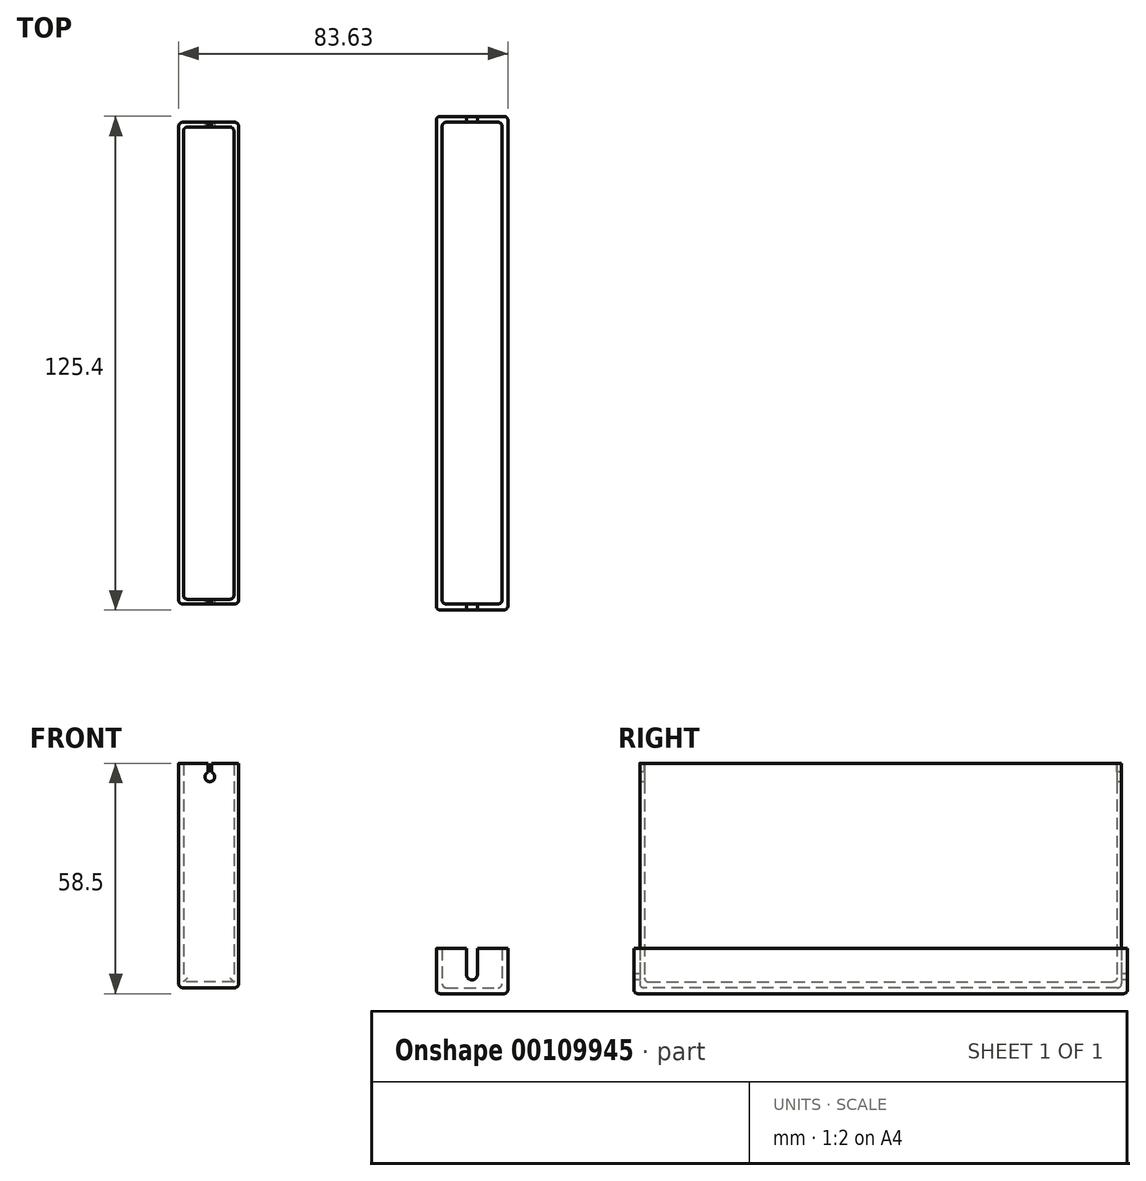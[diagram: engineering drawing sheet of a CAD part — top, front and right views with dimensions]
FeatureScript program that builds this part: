
annotation { "Feature Type Name" : "Feature", "Feature Type Description" : "" }
export const myFeature = defineFeature(function(context is Context, id is Id, definition is map)
    precondition{}
    {
        {
            var Q0;
            Q0=qCreatedBy(makeId("Top.planeOp"),FACE);
            var sketch = newSketch(context, id + "F0", { "sketchPlane" : qUnion([Q0])});
            skLineSegment(sketch, "E0.bottom", {"start": v(-47.39, 113) * mm, "end": v(-34.59, 113) * mm});
            skLineSegment(sketch, "E0.top", {"start": v(-47.39, -7) * mm, "end": v(-34.59, -7) * mm});
            skLineSegment(sketch, "E0.left", {"start": v(-47.39, 113) * mm, "end": v(-47.39, -7) * mm});
            skLineSegment(sketch, "E0.right", {"start": v(-34.59, 113) * mm, "end": v(-34.59, -7) * mm});
            skLineSegment(sketch, "E1.bottom", {"start": v(-48.59, 114.2) * mm, "end": v(-33.39, 114.2) * mm});
            skLineSegment(sketch, "E1.top", {"start": v(-48.59, -8.2) * mm, "end": v(-33.39, -8.2) * mm});
            skLineSegment(sketch, "E1.left", {"start": v(-48.59, 114.2) * mm, "end": v(-48.59, -8.2) * mm});
            skLineSegment(sketch, "E1.right", {"start": v(-33.39, 114.2) * mm, "end": v(-33.39, -8.2) * mm});
            skLineSegment(sketch, "E2.bottom", {"start": v(18.34, 114.2) * mm, "end": v(33.54, 114.2) * mm});
            skLineSegment(sketch, "E2.top", {"start": v(18.34, -8.2) * mm, "end": v(33.54, -8.2) * mm});
            skLineSegment(sketch, "E2.left", {"start": v(18.34, 114.2) * mm, "end": v(18.34, -8.2) * mm});
            skLineSegment(sketch, "E2.right", {"start": v(33.54, 114.2) * mm, "end": v(33.54, -8.2) * mm});
            skLineSegment(sketch, "E3.bottom", {"start": v(16.84, 115.7) * mm, "end": v(35.04, 115.7) * mm});
            skLineSegment(sketch, "E3.top", {"start": v(16.84, -9.7) * mm, "end": v(35.04, -9.7) * mm});
            skLineSegment(sketch, "E3.left", {"start": v(16.84, 115.7) * mm, "end": v(16.84, -9.7) * mm});
            skLineSegment(sketch, "E3.right", {"start": v(35.04, 115.7) * mm, "end": v(35.04, -9.7) * mm});
            skSolve(sketch);
        }
        {
            var Q0;
            Q0=makeQuery(id+"F0.imprint","IMPRINT",FACE,{"disambiguationData":[TD([[makeQuery(id+"F0.imprint","IMPRINT",EDGE,{"derivedFrom":sQuery(id+"F0.wireOp",EDGE,"E0.bottom")}),-1.0]])]});
            var Q1;
            Q1=makeQuery(id+"F0.imprint","IMPRINT",FACE,{"disambiguationData":[TD([[makeQuery(id+"F0.imprint","IMPRINT",EDGE,{"derivedFrom":sQuery(id+"F0.wireOp",EDGE,"E0.bottom")}),1.0]])]});
            extrude(context, id + "F1", {"entities" : qUnion([Q0, Q1]), "depth" : 1.5 * mm});
        }
        {
            var Q0;
            Q0=makeQuery(id+"F0.imprint","IMPRINT",FACE,{"disambiguationData":[TD([[makeQuery(id+"F0.imprint","IMPRINT",EDGE,{"derivedFrom":sQuery(id+"F0.wireOp",EDGE,"E0.bottom")}),1.0]])]});
            extrude(context, id + "F2", {"entities" : qUnion([Q0]), "operationType" : NewBodyOperationType.ADD, "depth" : 57 * mm});
        }
        {
            var Q0;
            {var subQ0=sQuery(id+"F0.wireOp",EDGE,"E1.top");Q0=makeQuery(id+"F2.boolean.opBoolean","MERGE",FACE,{"derivedFrom":[makeQuery(id+"F1.opExtrude","SWEPT_FACE",FACE,{"disambiguationData":[OSD([subQ0])]}),makeQuery(id+"F2.opExtrude","SWEPT_FACE",FACE,{"disambiguationData":[OSD([subQ0])]})]});}
            var sketch = newSketch(context, id + "F3", { "sketchPlane" : qUnion([Q0])});
            skCircle(sketch, "E4", {"center": v(-40.69, 53.6) * mm, "radius": 1.25 * mm});
            skLineSegment(sketch, "E5.bottom", {"start": v(-41.09, 57) * mm, "end": v(-40.29, 57) * mm});
            skLineSegment(sketch, "E5.top", {"start": v(-41.09, 53.6) * mm, "end": v(-40.29, 53.6) * mm});
            skLineSegment(sketch, "E5.left", {"start": v(-41.09, 57) * mm, "end": v(-41.09, 53.6) * mm});
            skLineSegment(sketch, "E5.right", {"start": v(-40.29, 57) * mm, "end": v(-40.29, 53.6) * mm});
            skSolve(sketch);
        }
        {
            var Q0;
            {var subQ5=sQuery(id+"F3.wireOp",EDGE,"E5.top");Q0=makeQuery(id+"F3.imprint","IMPRINT",FACE,{"disambiguationData":[TD([[makeQuery(id+"F3.imprint","IMPRINT",EDGE,{"derivedFrom":subQ5}),-1.0]])]});}
            var Q1;
            {var subQ5=sQuery(id+"F3.wireOp",EDGE,"E5.bottom");Q1=makeQuery(id+"F3.imprint","IMPRINT",FACE,{"disambiguationData":[TD([[makeQuery(id+"F3.imprint","IMPRINT",EDGE,{"derivedFrom":subQ5}),-1.0]])]});}
            var Q2;
            {var subQ5=sQuery(id+"F3.wireOp",EDGE,"E5.top");Q2=makeQuery(id+"F3.imprint","IMPRINT",FACE,{"disambiguationData":[TD([[makeQuery(id+"F3.imprint","IMPRINT",EDGE,{"derivedFrom":subQ5}),1.0]])]});}
            extrude(context, id + "F4", {"entities" : qUnion([Q0, Q1, Q2]), "operationType" : NewBodyOperationType.REMOVE, "endBound" : BoundingType.THROUGH_ALL, "oppositeDirection" : true, "depth" : 25 * mm});
        }
        {
            var Q0;
            Q0=makeQuery(id+"F0.imprint","IMPRINT",FACE,{"disambiguationData":[TD([[makeQuery(id+"F0.imprint","IMPRINT",EDGE,{"derivedFrom":sQuery(id+"F0.wireOp",EDGE,"E2.bottom")}),-1.0]])]});
            var Q1;
            Q1=makeQuery(id+"F0.imprint","IMPRINT",FACE,{"disambiguationData":[TD([[makeQuery(id+"F0.imprint","IMPRINT",EDGE,{"derivedFrom":sQuery(id+"F0.wireOp",EDGE,"E2.bottom")}),1.0]])]});
            extrude(context, id + "F5", {"entities" : qUnion([Q0, Q1]), "oppositeDirection" : true, "depth" : 1.5 * mm});
        }
        {
            var Q0;
            Q0=makeQuery(id+"F0.imprint","IMPRINT",FACE,{"disambiguationData":[TD([[makeQuery(id+"F0.imprint","IMPRINT",EDGE,{"derivedFrom":sQuery(id+"F0.wireOp",EDGE,"E2.bottom")}),1.0]])]});
            extrude(context, id + "F6", {"entities" : qUnion([Q0]), "operationType" : NewBodyOperationType.ADD, "depth" : 10 * mm});
        }
        {
            var Q0;
            {var subQ0=sQuery(id+"F0.wireOp",EDGE,"E3.top");Q0=makeQuery(id+"F6.boolean.opBoolean","MERGE",FACE,{"derivedFrom":[makeQuery(id+"F5.opExtrude","SWEPT_FACE",FACE,{"disambiguationData":[OSD([subQ0])]}),makeQuery(id+"F6.opExtrude","SWEPT_FACE",FACE,{"disambiguationData":[OSD([subQ0])]})]});}
            var sketch = newSketch(context, id + "F7", { "sketchPlane" : qUnion([Q0])});
            skPoint(sketch, "E6", {"position": v(25.9, 3.4) * mm});
            skCircle(sketch, "E7", {"center": v(25.9, 3.4) * mm, "radius": 1.4 * mm});
            skLineSegment(sketch, "E8.bottom", {"start": v(24.5, 3.48) * mm, "end": v(27.3, 3.48) * mm});
            skLineSegment(sketch, "E8.top", {"start": v(24.5, 10) * mm, "end": v(27.3, 10) * mm});
            skLineSegment(sketch, "E8.left", {"start": v(24.5, 3.48) * mm, "end": v(24.5, 10) * mm});
            skLineSegment(sketch, "E8.right", {"start": v(27.3, 3.48) * mm, "end": v(27.3, 10) * mm});
            skSolve(sketch);
        }
        {
            var Q0;
            {var subQ0=sQuery(id+"F7.wireOp",EDGE,"E8.bottom");var subQ1=sQuery(id+"F7.wireOp",EDGE,"E7");var subQ3=makeQuery(id+"F7.imprint","INTERSECT",VERTEX,{"derivedFrom":[subQ1,subQ0]});Q0=makeQuery(id+"F7.imprint","IMPRINT",FACE,{"disambiguationData":[TD([[makeQuery(id+"F7.imprint","IMPRINT",EDGE,{"disambiguationData":[TD([[subQ3,-1.0]])],"derivedFrom":subQ1}),1.0]])]});}
            var Q1;
            {var subQ0=sQuery(id+"F7.wireOp",EDGE,"E8.bottom");var subQ1=sQuery(id+"F7.wireOp",EDGE,"E7");var subQ3=makeQuery(id+"F7.imprint","INTERSECT",VERTEX,{"derivedFrom":[subQ1,subQ0]});Q1=makeQuery(id+"F7.imprint","IMPRINT",FACE,{"disambiguationData":[TD([[makeQuery(id+"F7.imprint","IMPRINT",EDGE,{"disambiguationData":[TD([[subQ3,1.0]])],"derivedFrom":subQ1}),1.0]])]});}
            var Q2;
            Q2=makeQuery(id+"F7.imprint","IMPRINT",FACE,{"disambiguationData":[TD([[makeQuery(id+"F7.imprint","IMPRINT",EDGE,{"derivedFrom":sQuery(id+"F7.wireOp",EDGE,"E8.top")}),-1.0]])]});
            extrude(context, id + "F8", {"entities" : qUnion([Q0, Q1, Q2]), "operationType" : NewBodyOperationType.REMOVE, "endBound" : BoundingType.THROUGH_ALL, "oppositeDirection" : true, "depth" : 25 * mm});
        }
        {
            var Q0;
            {var subQ0=sQuery(id+"F0.wireOp",EDGE,"E1.right");var subQ1=sQuery(id+"F0.wireOp",EDGE,"E1.top");Q0=makeQuery(id+"F2.boolean.opBoolean","MERGE",EDGE,{"derivedFrom":[makeQuery(id+"F1.opExtrude","SWEPT_EDGE",EDGE,{"disambiguationData":[OSD([subQ1,subQ0])]}),makeQuery(id+"F2.opExtrude","SWEPT_EDGE",EDGE,{"disambiguationData":[OSD([subQ1,subQ0])]})]});}
            var Q1;
            {var subQ0=sQuery(id+"F0.wireOp",EDGE,"E1.left");var subQ1=sQuery(id+"F0.wireOp",EDGE,"E1.top");Q1=makeQuery(id+"F2.boolean.opBoolean","MERGE",EDGE,{"derivedFrom":[makeQuery(id+"F1.opExtrude","SWEPT_EDGE",EDGE,{"disambiguationData":[OSD([subQ1,subQ0])]}),makeQuery(id+"F2.opExtrude","SWEPT_EDGE",EDGE,{"disambiguationData":[OSD([subQ1,subQ0])]})]});}
            var Q2;
            {var subQ0=sQuery(id+"F0.wireOp",EDGE,"E1.right");var subQ1=sQuery(id+"F0.wireOp",EDGE,"E1.bottom");Q2=makeQuery(id+"F2.boolean.opBoolean","MERGE",EDGE,{"derivedFrom":[makeQuery(id+"F1.opExtrude","SWEPT_EDGE",EDGE,{"disambiguationData":[OSD([subQ1,subQ0])]}),makeQuery(id+"F2.opExtrude","SWEPT_EDGE",EDGE,{"disambiguationData":[OSD([subQ1,subQ0])]})]});}
            var Q3;
            Q3=makeQuery(id+"F2.opExtrude","SWEPT_EDGE",EDGE,{"disambiguationData":[OSD([sQuery(id+"F0.wireOp",EDGE,"E0.bottom"),sQuery(id+"F0.wireOp",EDGE,"E0.left")])]});
            var Q4;
            {var subQ0=sQuery(id+"F0.wireOp",EDGE,"E1.left");var subQ1=sQuery(id+"F0.wireOp",EDGE,"E1.bottom");Q4=makeQuery(id+"F2.boolean.opBoolean","MERGE",EDGE,{"derivedFrom":[makeQuery(id+"F1.opExtrude","SWEPT_EDGE",EDGE,{"disambiguationData":[OSD([subQ1,subQ0])]}),makeQuery(id+"F2.opExtrude","SWEPT_EDGE",EDGE,{"disambiguationData":[OSD([subQ1,subQ0])]})]});}
            var Q5;
            Q5=makeQuery(id+"F2.opExtrude","SWEPT_EDGE",EDGE,{"disambiguationData":[OSD([sQuery(id+"F0.wireOp",EDGE,"E0.top"),sQuery(id+"F0.wireOp",EDGE,"E0.right")])]});
            var Q6;
            Q6=makeQuery(id+"F2.opExtrude","SWEPT_EDGE",EDGE,{"disambiguationData":[OSD([sQuery(id+"F0.wireOp",EDGE,"E0.top"),sQuery(id+"F0.wireOp",EDGE,"E0.left")])]});
            var Q7;
            Q7=makeQuery(id+"F2.opExtrude","SWEPT_EDGE",EDGE,{"disambiguationData":[OSD([sQuery(id+"F0.wireOp",EDGE,"E0.bottom"),sQuery(id+"F0.wireOp",EDGE,"E0.right")])]});
            var Q8;
            Q8=makeQuery(id+"F2.boolean.opBoolean","INTERSECT",EDGE,{"derivedFrom":[makeQuery(id+"F1.opExtrude","CAP_FACE",FACE,{"disambiguationData":[OSD([sQuery(id+"F0.wireOp",EDGE,"E1.bottom"),sQuery(id+"F0.wireOp",EDGE,"E1.top"),sQuery(id+"F0.wireOp",EDGE,"E1.left"),sQuery(id+"F0.wireOp",EDGE,"E1.right")])],"isStart":false}),makeQuery(id+"F2.opExtrude","SWEPT_FACE",FACE,{"disambiguationData":[OSD([sQuery(id+"F0.wireOp",EDGE,"E0.top")])]})]});
            var Q9;
            Q9=makeQuery(id+"F2.boolean.opBoolean","INTERSECT",EDGE,{"derivedFrom":[makeQuery(id+"F1.opExtrude","CAP_FACE",FACE,{"disambiguationData":[OSD([sQuery(id+"F0.wireOp",EDGE,"E1.bottom"),sQuery(id+"F0.wireOp",EDGE,"E1.top"),sQuery(id+"F0.wireOp",EDGE,"E1.left"),sQuery(id+"F0.wireOp",EDGE,"E1.right")])],"isStart":false}),makeQuery(id+"F2.opExtrude","SWEPT_FACE",FACE,{"disambiguationData":[OSD([sQuery(id+"F0.wireOp",EDGE,"E0.bottom")])]})]});
            var Q10;
            Q10=makeQuery(id+"F1.opExtrude","CAP_EDGE",EDGE,{"disambiguationData":[OSD([sQuery(id+"F0.wireOp",EDGE,"E1.top")])],"isStart":true});
            var Q11;
            Q11=makeQuery(id+"F1.opExtrude","CAP_EDGE",EDGE,{"disambiguationData":[OSD([sQuery(id+"F0.wireOp",EDGE,"E1.bottom")])],"isStart":true});
            var Q12;
            Q12=makeQuery(id+"F1.opExtrude","CAP_EDGE",EDGE,{"disambiguationData":[OSD([sQuery(id+"F0.wireOp",EDGE,"E1.left")])],"isStart":true});
            var Q13;
            Q13=makeQuery(id+"F1.opExtrude","CAP_EDGE",EDGE,{"disambiguationData":[OSD([sQuery(id+"F0.wireOp",EDGE,"E1.right")])],"isStart":true});
            var Q14;
            Q14=makeQuery(id+"F5.opExtrude","CAP_FACE",FACE,{"disambiguationData":[OSD([sQuery(id+"F0.wireOp",EDGE,"E3.bottom"),sQuery(id+"F0.wireOp",EDGE,"E3.top"),sQuery(id+"F0.wireOp",EDGE,"E3.left"),sQuery(id+"F0.wireOp",EDGE,"E3.right")])],"isStart":true});
            var Q15;
            Q15=makeQuery(id+"F5.opExtrude","CAP_FACE",FACE,{"disambiguationData":[OSD([sQuery(id+"F0.wireOp",EDGE,"E3.bottom"),sQuery(id+"F0.wireOp",EDGE,"E3.top"),sQuery(id+"F0.wireOp",EDGE,"E3.left"),sQuery(id+"F0.wireOp",EDGE,"E3.right")])],"isStart":false});
            var Q16;
            {var subQ0=sQuery(id+"F0.wireOp",EDGE,"E3.right");var subQ1=sQuery(id+"F0.wireOp",EDGE,"E3.top");Q16=makeQuery(id+"F6.boolean.opBoolean","MERGE",EDGE,{"derivedFrom":[makeQuery(id+"F5.opExtrude","SWEPT_EDGE",EDGE,{"disambiguationData":[OSD([subQ1,subQ0])]}),makeQuery(id+"F6.opExtrude","SWEPT_EDGE",EDGE,{"disambiguationData":[OSD([subQ1,subQ0])]})]});}
            var Q17;
            {var subQ0=sQuery(id+"F0.wireOp",EDGE,"E3.left");var subQ1=sQuery(id+"F0.wireOp",EDGE,"E3.top");Q17=makeQuery(id+"F6.boolean.opBoolean","MERGE",EDGE,{"derivedFrom":[makeQuery(id+"F5.opExtrude","SWEPT_EDGE",EDGE,{"disambiguationData":[OSD([subQ1,subQ0])]}),makeQuery(id+"F6.opExtrude","SWEPT_EDGE",EDGE,{"disambiguationData":[OSD([subQ1,subQ0])]})]});}
            var Q18;
            {var subQ0=sQuery(id+"F0.wireOp",EDGE,"E3.right");var subQ1=sQuery(id+"F0.wireOp",EDGE,"E3.bottom");Q18=makeQuery(id+"F6.boolean.opBoolean","MERGE",EDGE,{"derivedFrom":[makeQuery(id+"F5.opExtrude","SWEPT_EDGE",EDGE,{"disambiguationData":[OSD([subQ1,subQ0])]}),makeQuery(id+"F6.opExtrude","SWEPT_EDGE",EDGE,{"disambiguationData":[OSD([subQ1,subQ0])]})]});}
            var Q19;
            {var subQ0=sQuery(id+"F0.wireOp",EDGE,"E3.left");var subQ1=sQuery(id+"F0.wireOp",EDGE,"E3.bottom");Q19=makeQuery(id+"F6.boolean.opBoolean","MERGE",EDGE,{"derivedFrom":[makeQuery(id+"F5.opExtrude","SWEPT_EDGE",EDGE,{"disambiguationData":[OSD([subQ1,subQ0])]}),makeQuery(id+"F6.opExtrude","SWEPT_EDGE",EDGE,{"disambiguationData":[OSD([subQ1,subQ0])]})]});}
            var Q20;
            Q20=makeQuery(id+"F6.opExtrude","SWEPT_EDGE",EDGE,{"disambiguationData":[OSD([sQuery(id+"F0.wireOp",EDGE,"E2.top"),sQuery(id+"F0.wireOp",EDGE,"E2.left")])]});
            var Q21;
            Q21=makeQuery(id+"F6.opExtrude","SWEPT_EDGE",EDGE,{"disambiguationData":[OSD([sQuery(id+"F0.wireOp",EDGE,"E2.top"),sQuery(id+"F0.wireOp",EDGE,"E2.right")])]});
            var Q22;
            Q22=makeQuery(id+"F6.opExtrude","SWEPT_EDGE",EDGE,{"disambiguationData":[OSD([sQuery(id+"F0.wireOp",EDGE,"E2.bottom"),sQuery(id+"F0.wireOp",EDGE,"E2.left")])]});
            var Q23;
            Q23=makeQuery(id+"F6.opExtrude","SWEPT_EDGE",EDGE,{"disambiguationData":[OSD([sQuery(id+"F0.wireOp",EDGE,"E2.bottom"),sQuery(id+"F0.wireOp",EDGE,"E2.right")])]});
            fillet(context, id + "F9", {"entities" : qUnion([Q0, Q1, Q2, Q3, Q4, Q5, Q6, Q7, Q8, Q9, Q10, Q11, Q12, Q13, Q14, Q15, Q16, Q17, Q18, Q19, Q20, Q21, Q22, Q23]), "radius" : 1 * mm, "tangentPropagation" : true, "allowEdgeOverflow" : false});
        }
    });
